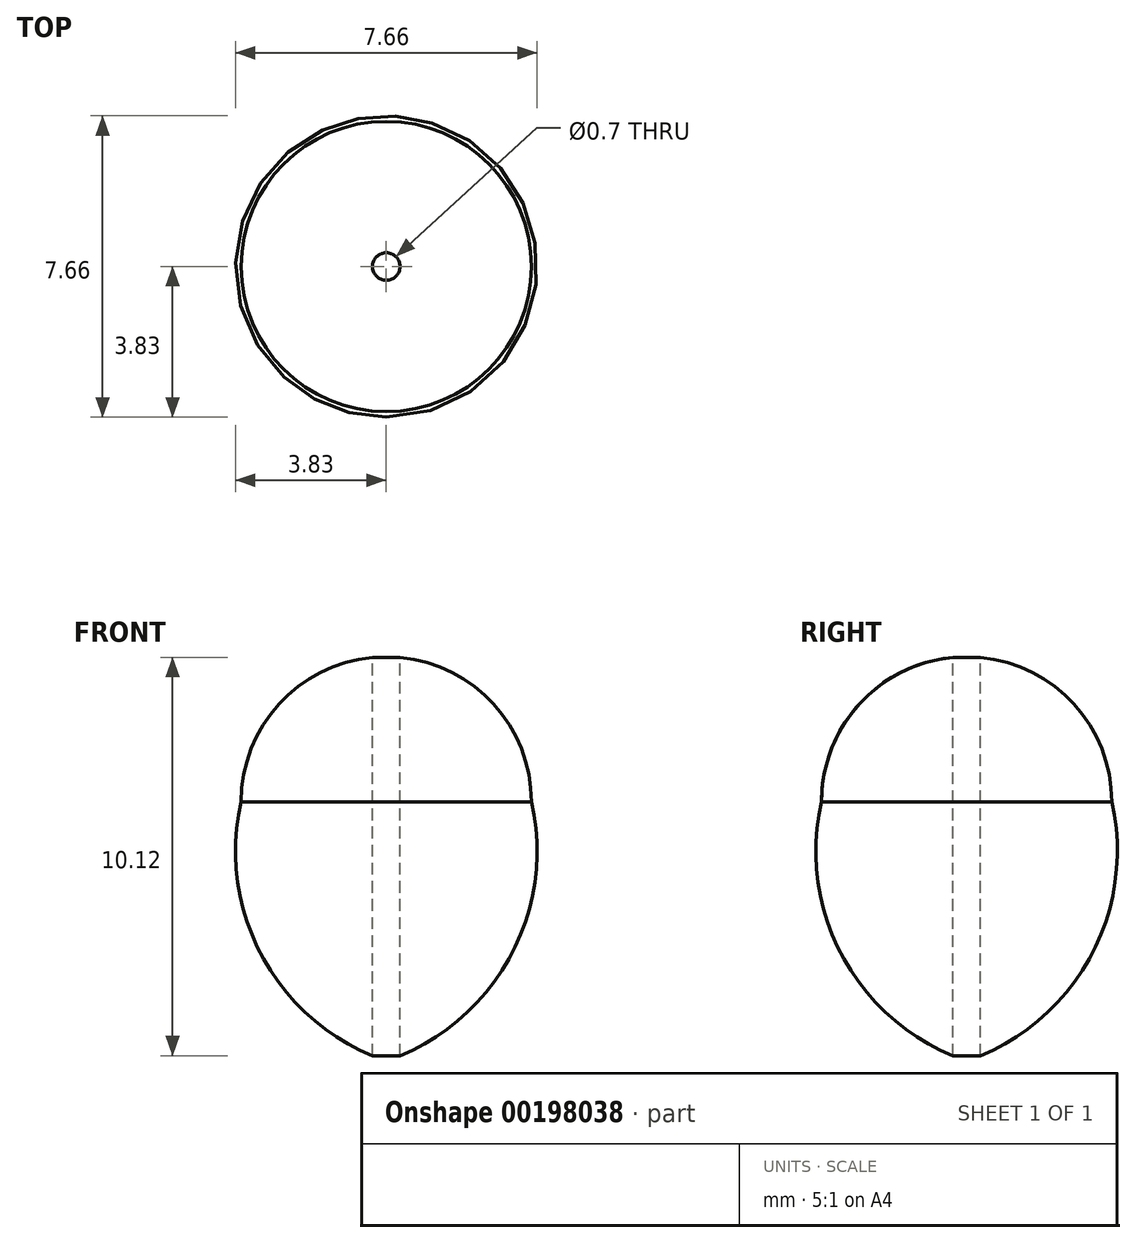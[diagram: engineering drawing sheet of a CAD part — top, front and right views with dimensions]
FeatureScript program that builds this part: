
annotation { "Feature Type Name" : "Feature", "Feature Type Description" : "" }
export const myFeature = defineFeature(function(context is Context, id is Id, definition is map)
    precondition{}
    {
        {
            var Q0;
            Q0=qCreatedBy(makeId("Right.planeOp"),FACE);
            var sketch = newSketch(context, id + "F0", { "sketchPlane" : qUnion([Q0])});
            skArc(sketch, "E0", {"start": v(3.34, 0) * mm, "mid": v(2.38, 2.48) * mm, "end": v(0, 3.67) * mm});
            skArc(sketch, "E1", {"start": v(0, -6.45) * mm, "mid": v(2.85, -3.84) * mm, "end": v(3.34, 0) * mm});
            skLineSegment(sketch, "E2", {"start": v(-0.35, 6.02) * mm, "end": v(-0.35, -7.53) * mm, "construction": true});
            skLineSegment(sketch, "E3", {"start": v(0, 3.67) * mm, "end": v(0, -6.45) * mm});
            skSolve(sketch);
        }
        {
            var Q0;
            Q0=makeQuery(id+"F0.imprint","IMPRINT",FACE,{"disambiguationData":[TD([[makeQuery(id+"F0.imprint","IMPRINT",EDGE,{"derivedFrom":sQuery(id+"F0.wireOp",EDGE,"E0")}),1.0]])]});
            var Q1;
            Q1=sQuery(id+"F0.wireOp",EDGE,"E0");
            var Q2;
            Q2=sQuery(id+"F0.wireOp",EDGE,"E1");
            var Q3;
            Q3=sQuery(id+"F0.wireOp",EDGE,"E2");
            revolve(context, id + "F1", {"entities" : qUnion([Q0]), "surfaceEntities" : qUnion([Q1, Q2]), "axis" : qUnion([Q3]), "revolveType" : RevolveType.FULL});
        }
    });
